# Revit family: Faucet-DXV-Percy-D351058XX_Series
name_source: partatom
category: Plumbing Fixtures
revit_build: Autodesk Revit 2014 (Build: 20130308_1515(x64)
units: mm (PartAtom-declared; Revit-internal decimal feet)

## types (10) — shared parameters
Assembly Code = D2020300
CW Connection = Yes
CWFU = 1.5
Cold Water Connection Diameter = 1/2"
Default Elevation = 0"
Description = Percy Widespread Faucet
HW Connection = Yes
HWFU = 1.5
Height = 10"
Hot Water Connection Diameter = 1"
Installation Type = Deck Mounted
Length = 5 7/16"
Manufacturer = DXV
Price = Prices may vary. Please consult Manufacturer Representative for most up-to-date price list.
Product Page URL = https://www.dxv.com
Revised Date = 05/07/2018
URL = http://www.dxv.com
Vent Connection = No
WFU = 2
Warranty Documentation Link = https://www.dxv.com
Waste Connection = No
Width = 8"

## per-type parameters (varying)
| type | ADA Compliant | Cross Handle Option | Finish | Flow Rate | Lever Handle Option | Material | Tri-Spoke Option |
| D35105800.144 | Yes | No | Metal-DXV-144-Brushed Nickel | 1.5 gpm (5.7L/min) | Yes | Metal-DXV-144-Brushed Nickel | No |
| D35105800.100 | Yes | No | Metal-DXV-100-Polished Chrome | 1.5 gpm (5.7L/min) | Yes | Metal-DXV-100-Polished Chrome | No |
| D35105840.100 | No | Yes | Metal-DXV-100-Polished Chrome | 1.5 gpm (5.7L/min) | No | Metal-DXV-100-Polished Chrome | No |
| D35105840.144 | No | Yes | Metal-DXV-144-Brushed Nickel | 1.5 gpm (5.7L/min) | No | Metal-DXV-144-Brushed Nickel | No |
| D3510580C.100 | Yes | No | Metal-DXV-100-Polished Chrome | 1.2 gpm (4.5 L/min) | Yes | Metal-DXV-100-Polished Chrome | No |
| D3510580C.144 | Yes | No | Metal-DXV-144-Brushed Nickel | 1.2 gpm (4.5 L/min) | Yes | Metal-DXV-144-Brushed Nickel | No |
| D3510584C.100 | No | Yes | Metal-DXV-100-Polished Chrome | 1.2 gpm (4.5 L/min) | No | Metal-DXV-100-Polished Chrome | No |
| D3510584C.144 | No | Yes | Metal-DXV-144-Brushed Nickel | 1.2 gpm (4.5 L/min) | No | Metal-DXV-144-Brushed Nickel | No |
| D35105870.100 | No | No | Metal-DXV-100-Polished Chrome | 1.2 gpm (4.5 L/min) | No | Metal-DXV-100-Polished Chrome | Yes |
| D35105870.144 | No | No | Metal-DXV-144-Brushed Nickel | 1.2 gpm (4.5 L/min) | No | Metal-DXV-144-Brushed Nickel | Yes |

note: column(s) folded — value = type name in every type: Model

## geometry (parser evidence)
native form markers: Sweep x1
no freeform markers — native parametric forms only
